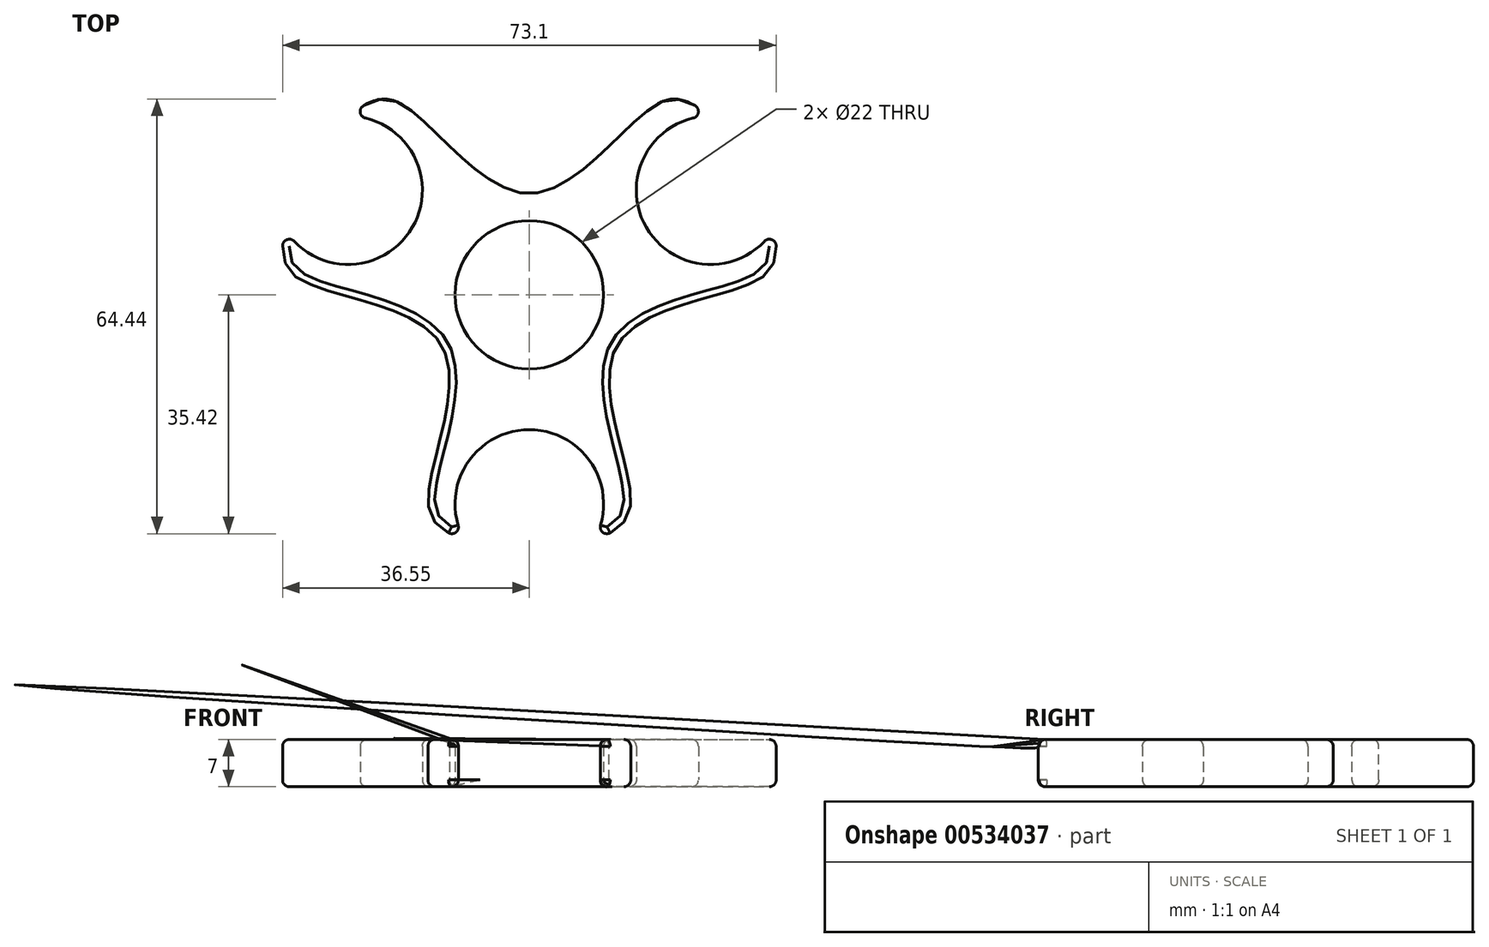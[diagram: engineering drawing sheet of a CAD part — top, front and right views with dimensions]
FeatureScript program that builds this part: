
annotation { "Feature Type Name" : "Feature", "Feature Type Description" : "" }
export const myFeature = defineFeature(function(context is Context, id is Id, definition is map)
    precondition{}
    {
        {
            var Q0;
            Q0=qCreatedBy(makeId("Top.planeOp"),FACE);
            var sketch = newSketch(context, id + "F0", { "sketchPlane" : qUnion([Q0])});
            skCircle(sketch, "E0", {"center": v(0, 0) * mm, "radius": 11 * mm});
            skLineSegment(sketch, "E1", {"start": v(0, -11) * mm, "end": v(0, -31) * mm, "construction": true});
            skLineSegment(sketch, "E2", {"start": v(9.53, 5.5) * mm, "end": v(26.85, 15.5) * mm, "construction": true});
            skLineSegment(sketch, "E3", {"start": v(-9.53, 5.5) * mm, "end": v(-26.85, 15.5) * mm, "construction": true});
            skPoint(sketch, "E4", {"position": v(0, -11) * mm});
            skPoint(sketch, "E5", {"position": v(9.53, 5.5) * mm});
            skPoint(sketch, "E6", {"position": v(-9.53, 5.5) * mm});
            skCircle(sketch, "E7", {"center": v(26.85, 15.5) * mm, "radius": 11 * mm});
            skCircle(sketch, "E8", {"center": v(-26.85, 15.5) * mm, "radius": 11 * mm});
            skLineSegment(sketch, "E9", {"start": v(26.85, 15.5) * mm, "end": v(36.37, 10) * mm, "construction": true});
            skLineSegment(sketch, "E10", {"start": v(26.85, 15.5) * mm, "end": v(26.85, 26.5) * mm, "construction": true});
            skPoint(sketch, "E11.endSnap0", {"position": v(254, -33.75) * mm});
            skLineSegment(sketch, "E12", {"start": v(-26.85, 15.5) * mm, "end": v(-26.85, 26.5) * mm, "construction": true});
            skPoint(sketch, "E11.end.orphan", {"position": v(-127, -33.75) * mm});
            skPoint(sketch, "E13.orphan", {"position": v(508, -36.5) * mm});
            skCircle(sketch, "E14", {"center": v(0, -31) * mm, "radius": 11 * mm});
            skLineSegment(sketch, "E15", {"start": v(0, -31) * mm, "end": v(9.53, -36.5) * mm, "construction": true});
            skLineSegment(sketch, "E16", {"start": v(0, -31) * mm, "end": v(-9.53, -36.5) * mm, "construction": true});
            skLineSegment(sketch, "E17", {"start": v(-26.85, 15.5) * mm, "end": v(-36.37, 10) * mm, "construction": true});
            skLineSegment(sketch, "E18", {"start": v(0, 0) * mm, "end": v(0, 15) * mm, "construction": true});
            skPoint(sketch, "E19.orphan", {"position": v(19.05, -11) * mm});
            skPoint(sketch, "E20.end.orphan", {"position": v(-42.09, -11) * mm});
            skLineSegment(sketch, "E21", {"start": v(0, 0) * mm, "end": v(13, -7.5) * mm, "construction": true});
            skLineSegment(sketch, "E22", {"start": v(0, 0) * mm, "end": v(-13, -7.5) * mm, "construction": true});
            skLineSegment(sketch, "E23", {"start": v(0, -31) * mm, "end": v(15, -31) * mm, "construction": true});
            skLineSegment(sketch, "E24", {"start": v(0, -31) * mm, "end": v(-15, -31) * mm, "construction": true});
            skLineSegment(sketch, "E25", {"start": v(26.85, 15.5) * mm, "end": v(34.35, 2.5) * mm, "construction": true});
            skLineSegment(sketch, "E26", {"start": v(26.85, 15.5) * mm, "end": v(19.35, 28.5) * mm, "construction": true});
            skLineSegment(sketch, "E27", {"start": v(-26.85, 15.5) * mm, "end": v(-34.35, 2.5) * mm, "construction": true});
            skLineSegment(sketch, "E28", {"start": v(-26.85, 15.5) * mm, "end": v(-19.35, 28.5) * mm, "construction": true});
            skFitSpline(sketch, "E29", {"points": [v(-36.37, 10) * mm, v(-34.35, 2.5) * mm, v(-13, -7.5) * mm, v(-15, -31) * mm, v(-9.53, -36.5) * mm], "startDerivative": vector(-4.67, -53.36) * mm, "endDerivative": vector(48.55, -22.64) * mm});
            skFitSpline(sketch, "E30", {"points": [v(9.53, -36.5) * mm, v(15, -31) * mm, v(13, -7.5) * mm, v(34.35, 2.5) * mm, v(36.37, 10) * mm], "startDerivative": vector(48.55, 22.64) * mm, "endDerivative": vector(-4.67, 53.36) * mm});
            skFitSpline(sketch, "E31", {"points": [v(-26.85, 26.5) * mm, v(-19.35, 28.5) * mm, v(0, 15) * mm, v(19.35, 28.5) * mm, v(26.85, 26.5) * mm], "startDerivative": vector(43.88, 30.72) * mm, "endDerivative": vector(43.88, -30.72) * mm});
            skSolve(sketch);
        }
        {
            var Q0;
            Q0=makeQuery(id+"F0.imprint","IMPRINT",FACE,{"disambiguationData":[TD([[makeQuery(id+"F0.imprint","IMPRINT",EDGE,{"derivedFrom":sQuery(id+"F0.wireOp",EDGE,"E0")}),-1.0]])]});
            extrude(context, id + "F1", {"entities" : qUnion([Q0]), "endBound" : BoundingType.SYMMETRIC, "depth" : 7 * mm, "offsetDistance" : 25.4 * mm});
        }
        {
            var Q0;
            Q0=makeQuery(id+"F1.opExtrude","CAP_EDGE",EDGE,{"disambiguationData":[OSD([sQuery(id+"F0.wireOp",EDGE,"E30")])],"isStart":false});
            var Q1;
            Q1=makeQuery(id+"F1.opExtrude","CAP_EDGE",EDGE,{"disambiguationData":[OSD([sQuery(id+"F0.wireOp",EDGE,"E14")])],"isStart":false});
            var Q2;
            Q2=makeQuery(id+"F1.opExtrude","CAP_EDGE",EDGE,{"disambiguationData":[OSD([sQuery(id+"F0.wireOp",EDGE,"E31")])],"isStart":false});
            var Q3;
            Q3=makeQuery(id+"F1.opExtrude","CAP_FACE",FACE,{"disambiguationData":[OSD([sQuery(id+"F0.wireOp",EDGE,"E0"),sQuery(id+"F0.wireOp",EDGE,"E7"),sQuery(id+"F0.wireOp",EDGE,"E8"),sQuery(id+"F0.wireOp",EDGE,"E14"),sQuery(id+"F0.wireOp",EDGE,"E29"),sQuery(id+"F0.wireOp",EDGE,"E30"),sQuery(id+"F0.wireOp",EDGE,"E31")])],"isStart":false});
            var Q4;
            Q4=makeQuery(id+"F1.opExtrude","CAP_FACE",FACE,{"disambiguationData":[OSD([sQuery(id+"F0.wireOp",EDGE,"E0"),sQuery(id+"F0.wireOp",EDGE,"E7"),sQuery(id+"F0.wireOp",EDGE,"E8"),sQuery(id+"F0.wireOp",EDGE,"E14"),sQuery(id+"F0.wireOp",EDGE,"E29"),sQuery(id+"F0.wireOp",EDGE,"E30"),sQuery(id+"F0.wireOp",EDGE,"E31")])],"isStart":true});
            var Q5;
            Q5=makeQuery(id+"F1.opExtrude","SWEPT_EDGE",EDGE,{"disambiguationData":[OSD([sQuery(id+"F0.wireOp",EDGE,"E7"),sQuery(id+"F0.wireOp",EDGE,"E30")])]});
            var Q6;
            Q6=makeQuery(id+"F1.opExtrude","SWEPT_EDGE",EDGE,{"disambiguationData":[OSD([sQuery(id+"F0.wireOp",EDGE,"E7"),sQuery(id+"F0.wireOp",EDGE,"E31")])]});
            var Q7;
            Q7=makeQuery(id+"F1.opExtrude","SWEPT_EDGE",EDGE,{"disambiguationData":[OSD([sQuery(id+"F0.wireOp",EDGE,"E8"),sQuery(id+"F0.wireOp",EDGE,"E31")])]});
            var Q8;
            Q8=makeQuery(id+"F1.opExtrude","SWEPT_EDGE",EDGE,{"disambiguationData":[OSD([sQuery(id+"F0.wireOp",EDGE,"E8"),sQuery(id+"F0.wireOp",EDGE,"E29")])]});
            fillet(context, id + "F2", {"entities" : qUnion([Q0, Q1, Q2, Q3, Q4, Q5, Q6, Q7, Q8]), "radius" : 1 * mm, "tangentPropagation" : true, "allowEdgeOverflow" : false});
        }
        {
            var Q0;
            Q0=makeQuery(id+"F1.opExtrude","SWEPT_EDGE",EDGE,{"disambiguationData":[OSD([sQuery(id+"F0.wireOp",EDGE,"E14"),sQuery(id+"F0.wireOp",EDGE,"E29")])]});
            var Q1;
            Q1=makeQuery(id+"F1.opExtrude","SWEPT_EDGE",EDGE,{"disambiguationData":[OSD([sQuery(id+"F0.wireOp",EDGE,"E14"),sQuery(id+"F0.wireOp",EDGE,"E30")])]});
            fillet(context, id + "F3", {"entities" : qUnion([Q0, Q1]), "radius" : 1 * mm, "tangentPropagation" : true, "allowEdgeOverflow" : false});
        }
    });
